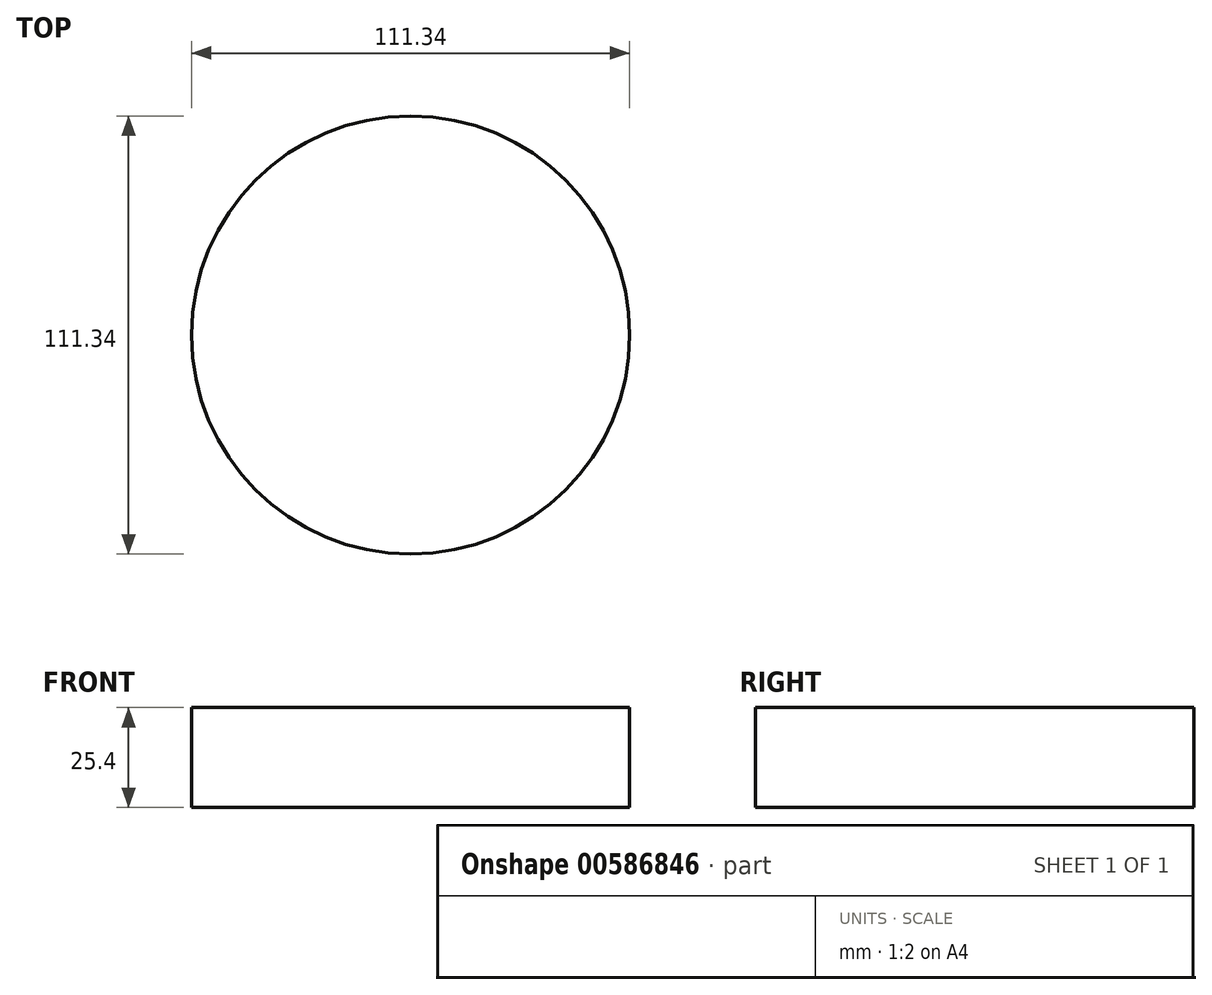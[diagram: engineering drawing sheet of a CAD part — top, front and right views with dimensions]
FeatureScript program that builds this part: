
annotation { "Feature Type Name" : "Feature", "Feature Type Description" : "" }
export const myFeature = defineFeature(function(context is Context, id is Id, definition is map)
    precondition{}
    {
        {
            var Q0;
            Q0=qCreatedBy(makeId("Top.planeOp"),FACE);
            var sketch = newSketch(context, id + "F0", { "sketchPlane" : qUnion([Q0])});
            skCircle(sketch, "E0", {"center": v(0, 0) * mm, "radius": 55.67 * mm});
            skSolve(sketch);
        }
        {
            var Q0;
            Q0=makeQuery(id+"F0.imprint","IMPRINT",FACE,{"disambiguationData":[TD([[makeQuery(id+"F0.imprint","IMPRINT",EDGE,{"derivedFrom":sQuery(id+"F0.wireOp",EDGE,"E0")}),1.0]])]});
            extrude(context, id + "F1", {"entities" : qUnion([Q0]), "depth" : 25.4 * mm, "offsetDistance" : 25.4 * mm});
        }
    });
